# Revit family: 56470113
name_source: partatom
category: Plumbing Fixtures
revit_build: Autodesk Revit 2017 (Build: 20190508_0315(x64)
units: mm (PartAtom-declared; Revit-internal decimal feet)

## family parameters
Always vertical = Yes
Cut with Voids When Loaded = No
OmniClass Number = 23.45.55.00
OmniClass Title = Sanitary Faucets, Wastes
Part Type = Normal
Room Calculation Point = No
Round Connector Dimension = Use Diameter
Shared = No
Work Plane-Based = No

## types (1)
- 56470113 Shower faucet
    2D/3D/BIM Files URL = http://static.hansa.com
    AssetType = Fixed
    BIMObjectName = 56470113
    Backflow Prevention EN1717 = EB
    BodyMaterial = Brass
    Brand = Hansa
    Catalog Drawing URL = http://static.hansa.com
    Category = Bathroom, shower
    Class = Single lever
    CloseOffRating = 0
    Color = Chrome
    Connection = Eccentric unions
    Connection Size = G1/2
    ConvergoRefNr = 0087-1909-0096-FI
    Customs Code = 84818011
    DN Size = DN15
    Dimension Drawing URL = http://static.hansa.com
    DurationUnit = Year
    EAN Number = 4057304012259
    EN Standard = EN 817
    FDV Document URL = http://www.hansa.com
    FaucetMainMaterial = Brass
    Features = Single lever
    Finish = Polished
    Flow Drawing URL = http://static.hansa.com
    Flow Rate At 300kPa = 0.3 L/s
    FlowCoefficient = 0
    Group = Shower faucets
    IfcExportAs = IfcValveType
    IfcExportType = FAUCET
    Installation Type = Wall-mounted
    Installation Width = CC150 ± 15 mm
    Installation and Maintenance = http://static.hansa.com
    Lever Handle = Lever with H+C symbol
    ManufacterURL = http://www.hansa.com
    Manufacturer = Hansa
    ManufacturerName = Hansa
    Market = AUT;ITA;FRA;CHE;ESP
    Material = Brass
    Max. Hot Water Supply = 90 °C
    Mechanical Parts = Non-return valve(s)
    Model = 56470113 Shower faucet
    ModelReference = 56470113
    NBSDescription = Water supply fittings for baths
    NBSReference = 45-35-70/315
    Name = 56470113 Shower faucet
    Name_en = 56470113 Shower faucet
    Noise Class = I(ISO 3822)
    NominalDepth = 196 mm
    NominalHeight = 104 mm  [stored 0.341207 ft]
    NominalWidth = 220 mm
    Package Weight = 1.525 kg
    Package external Dimensions = 200 x 165 x 95
    Product Code = 56470113
    Product Datasheet = http://www.hansa.com
    Product Family = HANSAPALENO
    Product Image URL = http://static.hansa.com
    Product URL = http://static.hansa.com
    Safety Sales Arguments = THERMO COOL. Improved safety – the housing of the fittings conducts minimal heat.
    Shape = Sculptured
    Size = 220x195x105 mm
    Spare Parts = http://static.hansa.com
    Temperature = Temperature limiter
    Uniclass2 = Pr_40_30_96_78
    Uniclass2015Description = Shower manual water supply sets
    Uniclass2015Reference = Pr_40_20_87_78
    Version = 1
    VersionDate = 23/07/2019
    WarrantyDescription = http://warranty.hansa.com
    WarrantyDurationUnit = Year
    WorkingPressure = 50 - 1000 kPa

note: [stored X ft] marks values corroborated as IEEE doubles in the binary element streams (Revit-internal decimal feet)

## geometry (parser evidence)
native form markers: Sweep x5
no freeform markers — native parametric forms only
